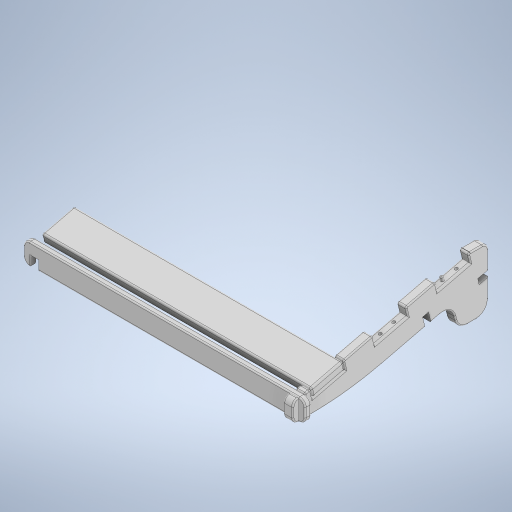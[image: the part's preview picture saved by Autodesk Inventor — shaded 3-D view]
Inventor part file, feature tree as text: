
AUTODESK INVENTOR PART (.ipt)
format: ipt  version: 2023 (Build 270158030, 158C)  size: 687,616 bytes
history: native  units: mm
features: fillet x17, extrude x11, sketch x10, other x4
ambient origin geometry x8: Origin, YZ Plane, XZ Plane, XY Plane, X Axis, Y Axis, Z Axis, Center Point
bodies: Body1 (feature_tree), Body2 (feature_tree), Body3 (feature_tree), Body4 (feature_tree)
feature tree (42):
  other  "Side_A"
  extrude  "Extrusion1"  Depth=320.0mm
  extrude  "Extrusion2"  Depth=15.0mm TaperAngle=0.0deg
  extrude  "Extrusion3"  Depth=55.0mm
  extrude  "Extrusion4"  Depth=50.0mm
  extrude  "Extrusion5"  Depth=15.0mm
  extrude  "Extrusion6"  Depth=15.0mm
  extrude  "Extrusion7"  Depth=15.0mm
  extrude  "Extrusion8"  Depth=10.0mm
  fillet  "Fillet1"  Radius=15.0mm
  fillet  "Fillet2"  Radius=440.0mm
  fillet  "Fillet3"  Radius=15.0mm
  fillet  "Fillet4"  Radius=17.0mm
  fillet  "Fillet5"  Radius=10.0mm
  fillet  "Fillet6"  Radius=15.0mm
  fillet  "Fillet7"  Radius=15.0mm
  fillet  "Fillet8"  Radius=10.0mm
  fillet  "Fillet9"  Radius=10.0mm
  fillet  "Fillet10"  Radius=18.0mm
  fillet  "Fillet11"  Radius=10.0mm
  fillet  "Fillet12"  Radius=17.0mm
  fillet  "Fillet13"  Radius=35.0mm
  fillet  "Fillet14"  Radius=10.0mm
  fillet  "Fillet15"  Radius=20.0mm
  extrude  "Extrusion9"  Depth=10.0mm
  fillet  "Fillet16"  Radius=10.0mm
  extrude  "Extrusion10"  Depth=1.3mm
  extrude  "Extrusion11"  Depth=10.0mm
  fillet  "Fillet17"  Radius=18.0mm
  sketch  "Sketch2"  dims[d0=100.0mm d1=320.0mm]
  sketch  "Sketch3"  dims[d3=30.0mm d4=15.0mm d5=0.0mm]
  sketch  "Sketch4"  dims[d6=55.0mm d7=55.0mm]
  other  "CrossBar1"
  sketch  "Sketch5"  dims[d8=55.0mm d9=50.0mm]
  sketch  "Sketch6"  dims[d10=50.0mm d12=15.0mm]
  other  "End Foot"
  sketch  "Sketch7"  dims[d13=15.0mm d14=15.0mm]
  sketch  "Sketch8"  dims[d15=15.0mm d16=0.0mm d17=35.0mm]
  sketch  "Sketch9"  dims[d18=50.0mm d19=59.956952mm d20=15.0mm d21=0.0mm d22=440.0mm d23=15.0mm d24=0.0mm d25=17.0mm d26=10.0mm d28=15.0mm d29=0.0mm d33=15.0mm d34=10.0mm d35=10.0mm d36=0.0mm d37=18.0mm d38=10.0mm d39=17.0mm d40=35.0mm d41=10.0mm d42=0.0mm d46=20.0mm]
  sketch  "Sketch10"  dims[d49=35.0mm d50=29.12457mm d51=10.0mm]
  sketch  "Sketch11"  dims[d52=10.0mm d53=30.0mm d54=10.0mm d55=18.0mm d56=15.0mm d57=0.0mm d58=500.0mm d59=20.0mm d60=20.0mm d61=10.0mm d62=10.0mm d63=10.0mm d64=3.0mm d65=3.0mm d66=3.0mm d67=2.0mm d68=2.0mm d69=2.0mm d70=2.0mm d71=2.0mm d72=3.0mm d73=5.0mm d74=16.0mm d75=16.0mm d76=7.5mm d77=7.5mm d78=15.0mm d79=0.0mm d80=16.0mm d81=16.0mm d82=16.0mm d83=16.0mm d84=3.0mm d85=7.5mm d86=7.5mm d87=7.5mm d88=0.0mm d89=15.0mm d90=0.0mm d91=1.3mm]
  other  "5mm Dowl"
